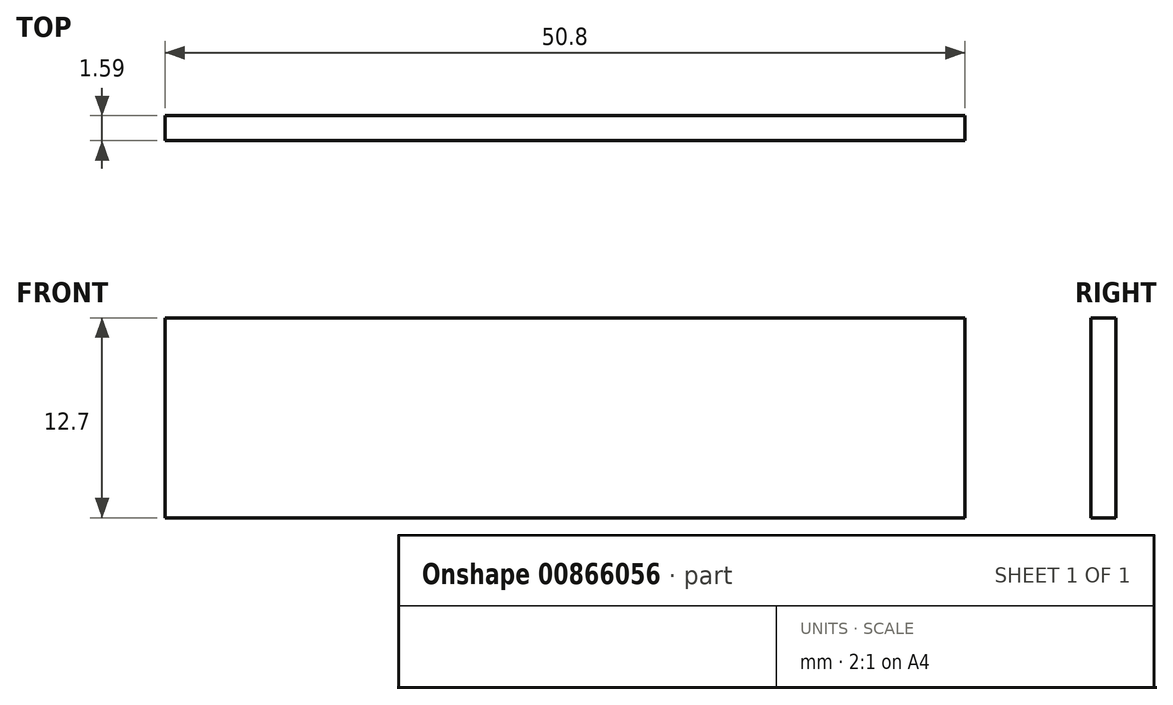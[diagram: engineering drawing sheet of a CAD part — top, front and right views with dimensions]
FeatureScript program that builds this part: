
annotation { "Feature Type Name" : "Feature", "Feature Type Description" : "" }
export const myFeature = defineFeature(function(context is Context, id is Id, definition is map)
    precondition{}
    {
        {
            var Q0;
            Q0=qCreatedBy(makeId("Front.planeOp"),FACE);
            var sketch = newSketch(context, id + "F0", { "sketchPlane" : qUnion([Q0])});
            skLineSegment(sketch, "E0.bottom", {"start": v(-35.94, 10.78) * mm, "end": v(14.86, 10.78) * mm});
            skLineSegment(sketch, "E0.top", {"start": v(-35.94, -1.92) * mm, "end": v(14.86, -1.92) * mm});
            skLineSegment(sketch, "E0.left", {"start": v(-35.94, 10.78) * mm, "end": v(-35.94, -1.92) * mm});
            skLineSegment(sketch, "E0.right", {"start": v(14.86, 10.78) * mm, "end": v(14.86, -1.92) * mm});
            skSolve(sketch);
        }
        {
            var Q0;
            Q0=makeQuery(id+"F0.imprint","IMPRINT",FACE,{"disambiguationData":[TD([[makeQuery(id+"F0.imprint","IMPRINT",EDGE,{"derivedFrom":sQuery(id+"F0.wireOp",EDGE,"E0.bottom")}),-1.0]])]});
            extrude(context, id + "F1", {"entities" : qUnion([Q0]), "depth" : 1.59 * mm, "offsetDistance" : 25.4 * mm});
        }
    });
